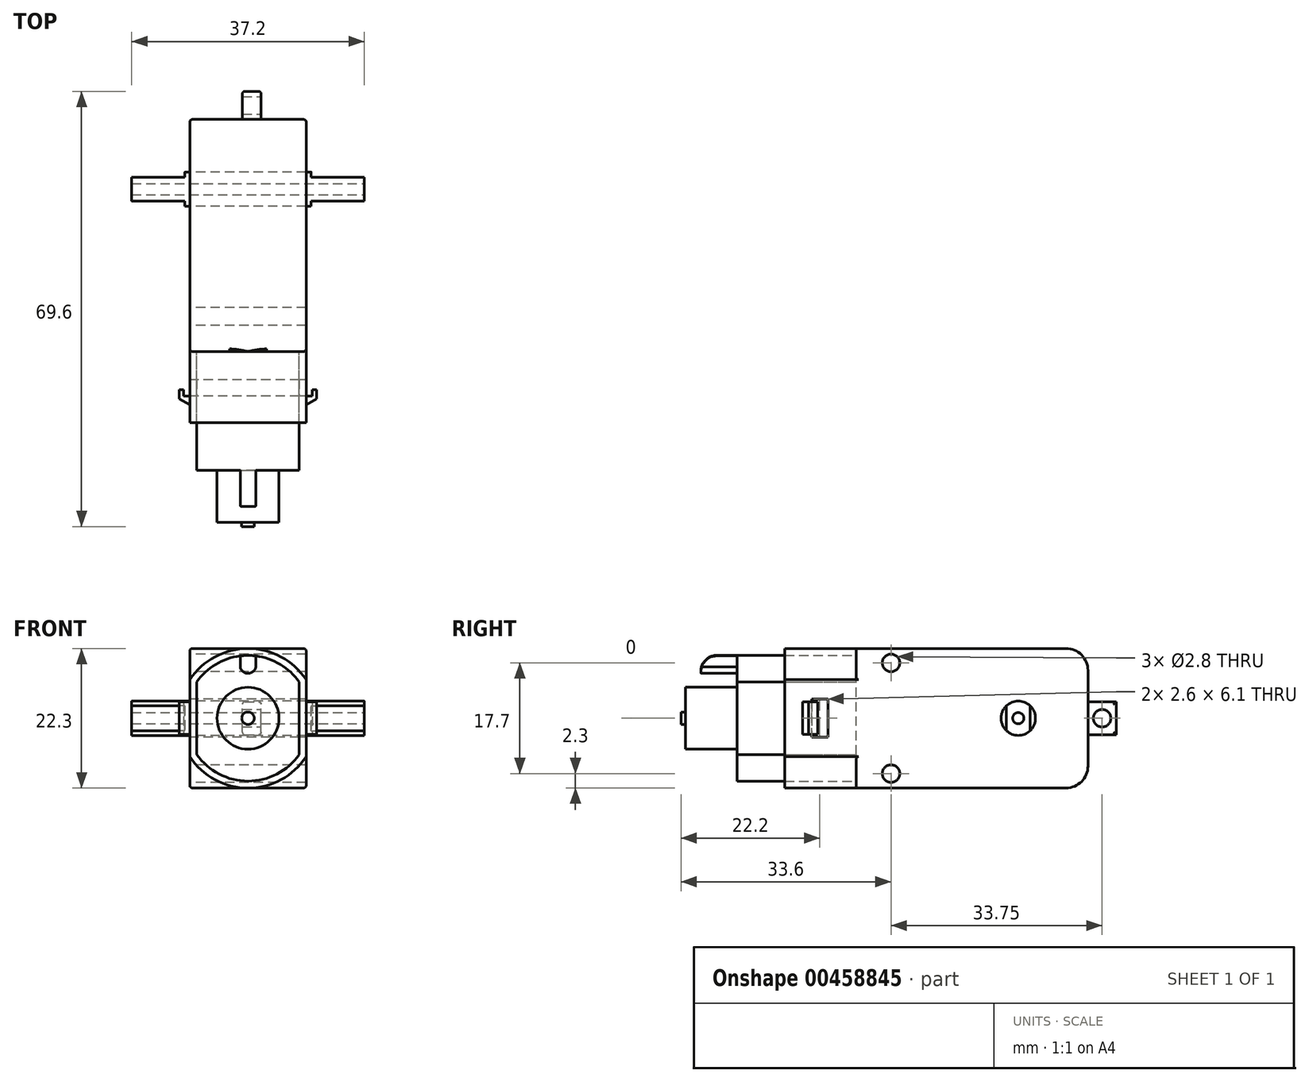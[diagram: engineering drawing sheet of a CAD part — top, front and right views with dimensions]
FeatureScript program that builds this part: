
annotation { "Feature Type Name" : "Feature", "Feature Type Description" : "" }
export const myFeature = defineFeature(function(context is Context, id is Id, definition is map)
    precondition{}
    {
        {
            var Q0;
            Q0=qCreatedBy(makeId("Front.planeOp"),FACE);
            var sketch = newSketch(context, id + "F0", { "sketchPlane" : qUnion([Q0])});
            skLineSegment(sketch, "E0.bottom", {"start": v(9.3, -11.15) * mm, "end": v(-9.3, -11.15) * mm});
            skLineSegment(sketch, "E0.top", {"start": v(9.3, 11.15) * mm, "end": v(-9.3, 11.15) * mm});
            skLineSegment(sketch, "E0.left", {"start": v(9.3, -11.15) * mm, "end": v(9.3, 11.15) * mm});
            skLineSegment(sketch, "E0.right", {"start": v(-9.3, -11.15) * mm, "end": v(-9.3, 11.15) * mm});
            skPoint(sketch, "E0.middle", {"position": v(0, 0) * mm});
            skSolve(sketch);
        }
        {
            var Q0;
            Q0 = qSketchRegion(id + "F0", true);
            extrude(context, id + "F1", {"entities" : qUnion([Q0]), "depth" : 37.1 * mm});
        }
        {
            var Q0;
            Q0=makeQuery(id+"F1.opExtrude","SWEPT_FACE",FACE,{"disambiguationData":[OSD([sQuery(id+"F0.wireOp",EDGE,"E0.right")])]});
            var sketch = newSketch(context, id + "F2", { "sketchPlane" : qUnion([Q0])});
            skCircle(sketch, "E1", {"center": v(31.5, -8.85) * mm, "radius": 1.4 * mm});
            skLineSegment(sketch, "E2", {"start": v(0, 0) * mm, "end": v(37.1, 0) * mm, "construction": true});
            skCircle(sketch, "E3.MirrorC", {"center": v(31.5, 8.85) * mm, "radius": 1.4 * mm});
            skCircle(sketch, "E4", {"center": v(11.15, 0) * mm, "radius": 2.75 * mm});
            skSolve(sketch);
        }
        {
            var Q0;
            Q0=makeQuery(id+"F1.opExtrude","CAP_FACE",FACE,{"disambiguationData":[OSD([sQuery(id+"F0.wireOp",EDGE,"E0.bottom"),sQuery(id+"F0.wireOp",EDGE,"E0.top"),sQuery(id+"F0.wireOp",EDGE,"E0.left"),sQuery(id+"F0.wireOp",EDGE,"E0.right")])],"isStart":false});
            var sketch = newSketch(context, id + "F3", { "sketchPlane" : qUnion([Q0])});
            skArc(sketch, "E5", {"start": v(-9.3, -6.15) * mm, "mid": v(0, -11.15) * mm, "end": v(9.3, -6.15) * mm});
            skLineSegment(sketch, "E6.0", {"start": v(9.3, -6.15) * mm, "end": v(9.3, 6.15) * mm});
            skLineSegment(sketch, "E6.1", {"start": v(-9.3, -6.15) * mm, "end": v(-9.3, 6.15) * mm});
            skArc(sketch, "E7.trimOffspring", {"start": v(9.3, 6.15) * mm, "mid": v(0, 11.15) * mm, "end": v(-9.3, 6.15) * mm});
            skPoint(sketch, "E8.orphan", {"position": v(-9.3, 11.15) * mm});
            skPoint(sketch, "E9.orphan", {"position": v(9.3, 11.15) * mm});
            skPoint(sketch, "E10.orphan", {"position": v(9.3, -11.15) * mm});
            skPoint(sketch, "E11.orphan", {"position": v(-9.3, -11.15) * mm});
            skArc(sketch, "E12.0", {"start": v(8.2, 5.81) * mm, "mid": v(0, 10.05) * mm, "end": v(-8.2, 5.81) * mm});
            skLineSegment(sketch, "E12.1", {"start": v(8.2, -5.81) * mm, "end": v(8.2, 5.81) * mm});
            skArc(sketch, "E12.2", {"start": v(-8.2, -5.81) * mm, "mid": v(0, -10.05) * mm, "end": v(8.2, -5.81) * mm});
            skLineSegment(sketch, "E12.3", {"start": v(-8.2, -5.81) * mm, "end": v(-8.2, 5.81) * mm});
            skSolve(sketch);
        }
        {
            var Q0;
            Q0 = qSketchRegion(id + "F3", true);
            extrude(context, id + "F4", {"entities" : qUnion([Q0]), "operationType" : NewBodyOperationType.ADD, "depth" : 11.4 * mm});
        }
        {
            var Q0;
            {var subQ0=sQuery(id+"F0.wireOp",EDGE,"F8vdl7xD-wS4J-gisc-z2d9-TpghqO1zXRkm");Q0=makeQuery(id+"F4.boolean.opBoolean","SPLIT",FACE,{"disambiguationData":[TD([makeQuery(id+"F1.opExtrude","SWEPT_FACE",FACE,{"disambiguationData":[OSD([subQ0])]}),makeQuery(id+"F4.opExtrude","SWEPT_FACE",FACE,{"disambiguationData":[OSD([sQuery(id+"F3.wireOp",EDGE,"E12.0")])]}),makeQuery(id+"F4.opExtrude","SWEPT_FACE",FACE,{"disambiguationData":[OSD([sQuery(id+"F3.wireOp",EDGE,"E12.1")])]}),makeQuery(id+"F4.opExtrude","SWEPT_FACE",FACE,{"disambiguationData":[OSD([sQuery(id+"F3.wireOp",EDGE,"E12.2")])]}),makeQuery(id+"F4.opExtrude","SWEPT_FACE",FACE,{"disambiguationData":[OSD([sQuery(id+"F3.wireOp",EDGE,"E12.3")])]})])],"derivedFrom":makeQuery(id+"F1.opExtrude","CAP_FACE",FACE,{"disambiguationData":[OSD([sQuery(id+"F0.wireOp",EDGE,"E0.bottom"),sQuery(id+"F0.wireOp",EDGE,"E0.top"),sQuery(id+"F0.wireOp",EDGE,"E0.left"),sQuery(id+"F0.wireOp",EDGE,"E0.right"),subQ0])],"isStart":false})});}
            var sketch = newSketch(context, id + "F5", { "sketchPlane" : qUnion([Q0])});
            skLineSegment(sketch, "E13.0", {"start": v(-8.2, -5.81) * mm, "end": v(-8.2, 5.81) * mm});
            skArc(sketch, "E13.1", {"start": v(8.2, 5.81) * mm, "mid": v(0, 10.05) * mm, "end": v(-8.2, 5.81) * mm});
            skLineSegment(sketch, "E13.2", {"start": v(8.2, -5.81) * mm, "end": v(8.2, 5.81) * mm});
            skArc(sketch, "E13.3", {"start": v(-8.2, -5.81) * mm, "mid": v(0, -10.05) * mm, "end": v(8.2, -5.81) * mm});
            skSolve(sketch);
        }
        {
            var Q0;
            Q0 = qSketchRegion(id + "F5", true);
            extrude(context, id + "F6", {"entities" : qUnion([Q0]), "depth" : 24.8 * mm});
        }
        {
            var Q0;
            Q0 = qSketchRegion(id + "F2", true);
            extrude(context, id + "F7", {"entities" : qUnion([Q0]), "operationType" : NewBodyOperationType.REMOVE, "oppositeDirection" : true, "depth" : 25 * mm});
        }
        {
            var Q0;
            Q0=qCreatedBy(makeId("Right.planeOp"),FACE);
            var sketch = newSketch(context, id + "F8", { "sketchPlane" : qUnion([Q0])});
            skCircle(sketch, "E14", {"center": v(-11.15, 0) * mm, "radius": 2.75 * mm});
            skSolve(sketch);
        }
        {
            var Q0;
            Q0 = qSketchRegion(id + "F8", true);
            extrude(context, id + "F9", {"entities" : qUnion([Q0]), "depth" : 37.2 * mm, "symmetric" : true});
        }
        {
            var Q0;
            Q0=makeQuery(id+"F9.opExtrude","CAP_FACE",FACE,{"disambiguationData":[OSD([sQuery(id+"F8.wireOp",EDGE,"E14")])],"isStart":false});
            var sketch = newSketch(context, id + "F10", { "sketchPlane" : qUnion([Q0])});
            skLineSegment(sketch, "E15", {"start": v(-9.25, -1.99) * mm, "end": v(-9.25, 1.99) * mm});
            skLineSegment(sketch, "E16", {"start": v(-13.05, -1.99) * mm, "end": v(-13.05, 1.99) * mm});
            skPoint(sketch, "E17.start.orphan", {"position": v(-8.4, 0) * mm});
            skArc(sketch, "E18.0", {"start": v(-9.25, -1.99) * mm, "mid": v(-8.4, 0) * mm, "end": v(-9.25, 1.99) * mm});
            skArc(sketch, "E19.trimOffspring", {"start": v(-13.05, 1.99) * mm, "mid": v(-13.9, 0) * mm, "end": v(-13.05, -1.99) * mm});
            skSolve(sketch);
        }
        {
            var Q0;
            Q0 = qSketchRegion(id + "F10", true);
            extrude(context, id + "F11", {"entities" : qUnion([Q0]), "operationType" : NewBodyOperationType.REMOVE, "oppositeDirection" : true, "depth" : 8.5 * mm});
        }
        {
            var Q0;
            Q0=makeQuery(id+"F9.opExtrude","CAP_FACE",FACE,{"disambiguationData":[OSD([sQuery(id+"F8.wireOp",EDGE,"E14")])],"isStart":true});
            var sketch = newSketch(context, id + "F12", { "sketchPlane" : qUnion([Q0])});
            skLineSegment(sketch, "E20", {"start": v(9.25, 1.99) * mm, "end": v(9.25, -1.99) * mm});
            skLineSegment(sketch, "E21", {"start": v(13.05, 1.99) * mm, "end": v(13.05, -1.99) * mm});
            skPoint(sketch, "E22.start.orphan", {"position": v(9.25, 0) * mm});
            skPoint(sketch, "E23.start.orphan", {"position": v(13.05, 0) * mm});
            skArc(sketch, "E24.0", {"start": v(9.25, 1.99) * mm, "mid": v(11.15, -2.75) * mm, "end": v(13.05, 1.99) * mm});
            skSolve(sketch);
        }
        {
            var Q0;
            Q0 = qSketchRegion(id + "F12", true);
            extrude(context, id + "F13", {"entities" : qUnion([Q0]), "operationType" : NewBodyOperationType.REMOVE, "oppositeDirection" : true, "depth" : 8.5 * mm});
        }
        {
            var Q0;
            Q0=makeQuery(id+"F1.opExtrude","CAP_FACE",FACE,{"disambiguationData":[OSD([sQuery(id+"F0.wireOp",EDGE,"E0.bottom"),sQuery(id+"F0.wireOp",EDGE,"E0.top"),sQuery(id+"F0.wireOp",EDGE,"E0.left"),sQuery(id+"F0.wireOp",EDGE,"E0.right")])],"isStart":true});
            var sketch = newSketch(context, id + "F14", { "sketchPlane" : qUnion([Q0])});
            skPoint(sketch, "E25.middle", {"position": v(-0.6, 0) * mm});
            skLineSegment(sketch, "E26.bottom", {"start": v(0.9, -2.63) * mm, "end": v(-2.1, -2.63) * mm});
            skLineSegment(sketch, "E26.top", {"start": v(0.9, 2.63) * mm, "end": v(-2.1, 2.63) * mm});
            skLineSegment(sketch, "E26.left", {"start": v(0.9, -2.63) * mm, "end": v(0.9, 2.63) * mm});
            skLineSegment(sketch, "E26.right", {"start": v(-2.1, -2.63) * mm, "end": v(-2.1, 2.63) * mm});
            skSolve(sketch);
        }
        {
            var Q0;
            Q0 = qSketchRegion(id + "F14", true);
            extrude(context, id + "F15", {"entities" : qUnion([Q0]), "operationType" : NewBodyOperationType.ADD, "depth" : 4.5 * mm});
        }
        {
            var Q0;
            Q0=makeQuery(id+"F4.boolean.opBoolean","MERGE",FACE,{"derivedFrom":[makeQuery(id+"F1.opExtrude","SWEPT_FACE",FACE,{"disambiguationData":[OSD([sQuery(id+"F0.wireOp",EDGE,"E0.right")])]}),makeQuery(id+"F4.opExtrude","SWEPT_FACE",FACE,{"disambiguationData":[OSD([sQuery(id+"F3.wireOp",EDGE,"E6.1")])]})]});
            var sketch = newSketch(context, id + "F16", { "sketchPlane" : qUnion([Q0])});
            skLineSegment(sketch, "E27.bottom", {"start": v(41.6, -3.05) * mm, "end": v(44.2, -3.05) * mm});
            skLineSegment(sketch, "E27.top", {"start": v(41.6, 3.05) * mm, "end": v(44.2, 3.05) * mm});
            skLineSegment(sketch, "E27.left", {"start": v(41.6, -3.05) * mm, "end": v(41.6, 3.05) * mm});
            skLineSegment(sketch, "E27.right", {"start": v(44.2, -3.05) * mm, "end": v(44.2, 3.05) * mm});
            skPoint(sketch, "E27.middle", {"position": v(42.9, 0) * mm});
            skSolve(sketch);
        }
        {
            var Q0;
            Q0=makeQuery(id+"F6.opExtrude","CAP_FACE",FACE,{"disambiguationData":[OSD([sQuery(id+"F5.wireOp",EDGE,"E13.0"),sQuery(id+"F5.wireOp",EDGE,"E13.1"),sQuery(id+"F5.wireOp",EDGE,"E13.2"),sQuery(id+"F5.wireOp",EDGE,"E13.3")])],"isStart":false});
            var sketch = newSketch(context, id + "F17", { "sketchPlane" : qUnion([Q0])});
            skCircle(sketch, "E28", {"center": v(0, 0) * mm, "radius": 4.95 * mm});
            skCircle(sketch, "E29", {"center": v(0, 0) * mm, "radius": 1 * mm});
            skSolve(sketch);
        }
        {
            var Q0;
            Q0=makeQuery(id+"F17.imprint","IMPRINT",FACE,{"disambiguationData":[TD([[makeQuery(id+"F17.imprint","IMPRINT",EDGE,{"derivedFrom":sQuery(id+"F17.wireOp",EDGE,"E29")}),1.0]])]});
            extrude(context, id + "F18", {"entities" : qUnion([Q0]), "operationType" : NewBodyOperationType.ADD, "depth" : 3.2 * mm});
        }
        {
            var Q0;
            Q0=makeQuery(id+"F17.imprint","IMPRINT",FACE,{"disambiguationData":[TD([[makeQuery(id+"F17.imprint","IMPRINT",EDGE,{"derivedFrom":sQuery(id+"F17.wireOp",EDGE,"E28")}),1.0]])]});
            extrude(context, id + "F19", {"entities" : qUnion([Q0]), "operationType" : NewBodyOperationType.ADD, "depth" : 2.5 * mm});
        }
        {
            var Q0;
            Q0=makeQuery(id+"F17.imprint","IMPRINT",FACE,{"disambiguationData":[TD([[makeQuery(id+"F17.imprint","IMPRINT",EDGE,{"derivedFrom":sQuery(id+"F17.wireOp",EDGE,"E28")}),-1.0]])]});
            var sketch = newSketch(context, id + "F20", { "sketchPlane" : qUnion([Q0])});
            skArc(sketch, "E30.0", {"start": v(-1.25, -9.97) * mm, "mid": v(0, -10.05) * mm, "end": v(1.25, -9.97) * mm});
            skLineSegment(sketch, "E31", {"start": v(-1.25, -9.97) * mm, "end": v(-1.25, -8.18) * mm});
            skLineSegment(sketch, "E32", {"start": v(1.25, -9.97) * mm, "end": v(1.25, -8.18) * mm});
            skArc(sketch, "E33", {"start": v(1.25, -8.18) * mm, "mid": v(0, -7.18) * mm, "end": v(-1.25, -8.18) * mm});
            skArc(sketch, "E34.MirrorCS", {"start": v(1.25, 8.18) * mm, "mid": v(0, 7.18) * mm, "end": v(-1.25, 8.18) * mm});
            skLineSegment(sketch, "E35.MirrorCS", {"start": v(1.25, 9.97) * mm, "end": v(1.25, 8.18) * mm});
            skLineSegment(sketch, "E36.MirrorCS", {"start": v(-1.25, 9.97) * mm, "end": v(-1.25, 8.18) * mm});
            skArc(sketch, "E37.0", {"start": v(1.25, 9.97) * mm, "mid": v(0, 10.05) * mm, "end": v(-1.25, 9.97) * mm});
            skPoint(sketch, "E38.orphan", {"position": v(-8.2, 5.81) * mm});
            skPoint(sketch, "E39.orphan", {"position": v(8.2, 5.81) * mm});
            skPoint(sketch, "E40.orphan", {"position": v(8.2, -5.81) * mm});
            skPoint(sketch, "E41.orphan", {"position": v(-8.2, -5.81) * mm});
            skSolve(sketch);
        }
        {
            var Q0;
            Q0=makeQuery(id+"F16.imprint","IMPRINT",FACE,{"disambiguationData":[TD([[makeQuery(id+"F16.imprint","IMPRINT",EDGE,{"derivedFrom":sQuery(id+"F16.wireOp",EDGE,"E27.bottom")}),1.0]])]});
            extrude(context, id + "F21", {"entities" : qUnion([Q0]), "operationType" : NewBodyOperationType.REMOVE, "oppositeDirection" : true, "depth" : 25 * mm});
        }
        {
            var Q0;
            Q0=qCreatedBy(makeId("Top.planeOp"),FACE);
            var sketch = newSketch(context, id + "F22", { "sketchPlane" : qUnion([Q0])});
            skPoint(sketch, "E42.0", {"position": v(-9.3, -44.2) * mm});
            skLineSegment(sketch, "E43", {"start": v(-9.3, -44.2) * mm, "end": v(-9.3, -45.65) * mm});
            skLineSegment(sketch, "E44", {"start": v(-9.3, -45.65) * mm, "end": v(-11, -44.7) * mm});
            skLineSegment(sketch, "E45", {"start": v(-11, -44.7) * mm, "end": v(-11, -43.2) * mm});
            skLineSegment(sketch, "E46", {"start": v(-11, -43.2) * mm, "end": v(-10.3, -43.2) * mm});
            skLineSegment(sketch, "E47", {"start": v(-10.3, -43.2) * mm, "end": v(-10.3, -44.2) * mm});
            skLineSegment(sketch, "E48", {"start": v(-10.3, -44.2) * mm, "end": v(-9.3, -44.2) * mm});
            skSolve(sketch);
        }
        {
            var Q0;
            Q0=makeQuery(id+"F22.imprint","IMPRINT",FACE,{"disambiguationData":[TD([[makeQuery(id+"F22.imprint","IMPRINT",EDGE,{"derivedFrom":sQuery(id+"F22.wireOp",EDGE,"E43")}),-1.0]])]});
            extrude(context, id + "F23", {"entities" : qUnion([Q0]), "operationType" : NewBodyOperationType.ADD, "depth" : 5.2 * mm, "symmetric" : true});
        }
        {
            var Q0;
            Q0=makeQuery(id+"F9.opExtrude","CAP_FACE",FACE,{"disambiguationData":[OSD([sQuery(id+"F8.wireOp",EDGE,"E14")])],"isStart":false});
            var sketch = newSketch(context, id + "F24", { "sketchPlane" : qUnion([Q0])});
            skCircle(sketch, "E49", {"center": v(-11.15, 0) * mm, "radius": 0.9 * mm});
            skSolve(sketch);
        }
        {
            var Q0;
            Q0 = qSketchRegion(id + "F24", true);
            extrude(context, id + "F25", {"entities" : qUnion([Q0]), "operationType" : NewBodyOperationType.REMOVE, "endBound" : BoundingType.THROUGH_ALL, "oppositeDirection" : true, "depth" : 25 * mm});
        }
        {
            var Q0;
            Q0=qCreatedBy(makeId("Top.planeOp"),FACE);
            var sketch = newSketch(context, id + "F26", { "sketchPlane" : qUnion([Q0])});
            skPoint(sketch, "E50.0", {"position": v(9.3, -44.2) * mm});
            skLineSegment(sketch, "E51", {"start": v(9.3, -44.2) * mm, "end": v(9.3, -45.65) * mm});
            skLineSegment(sketch, "E52", {"start": v(9.3, -45.65) * mm, "end": v(11, -44.7) * mm});
            skLineSegment(sketch, "E53", {"start": v(11, -44.7) * mm, "end": v(11, -43.2) * mm});
            skLineSegment(sketch, "E54", {"start": v(11, -43.2) * mm, "end": v(10.3, -43.2) * mm});
            skLineSegment(sketch, "E55", {"start": v(10.3, -43.2) * mm, "end": v(10.3, -44.2) * mm});
            skLineSegment(sketch, "E56", {"start": v(10.3, -44.2) * mm, "end": v(9.3, -44.2) * mm});
            skSolve(sketch);
        }
        {
            var Q0;
            Q0=makeQuery(id+"F26.imprint","IMPRINT",FACE,{"disambiguationData":[TD([[makeQuery(id+"F26.imprint","IMPRINT",EDGE,{"derivedFrom":sQuery(id+"F26.wireOp",EDGE,"E51")}),1.0]])]});
            extrude(context, id + "F27", {"entities" : qUnion([Q0]), "operationType" : NewBodyOperationType.ADD, "depth" : 5.2 * mm, "symmetric" : true});
        }
        {
            var Q0;
            Q0=makeQuery(id+"F20.imprint","IMPRINT",FACE,{"disambiguationData":[TD([[makeQuery(id+"F20.imprint","IMPRINT",EDGE,{"derivedFrom":sQuery(id+"F20.wireOp",EDGE,"E34.MirrorCS")}),-1.0]])]});
            var Q1;
            Q1=makeQuery(id+"F20.imprint","IMPRINT",FACE,{"disambiguationData":[TD([[makeQuery(id+"F20.imprint","IMPRINT",EDGE,{"derivedFrom":sQuery(id+"F20.wireOp",EDGE,"E30.0")}),1.0]])]});
            extrude(context, id + "F28", {"entities" : qUnion([Q0, Q1]), "operationType" : NewBodyOperationType.REMOVE, "oppositeDirection" : true, "depth" : 5.8 * mm});
        }
        {
            var Q0;
            Q0=makeQuery(id+"F15.opExtrude","SWEPT_FACE",FACE,{"disambiguationData":[OSD([sQuery(id+"F14.wireOp",EDGE,"E26.right")])]});
            var sketch = newSketch(context, id + "F29", { "sketchPlane" : qUnion([Q0])});
            skPoint(sketch, "E57.end.orphan", {"position": v(-4.5, 0) * mm});
            skPoint(sketch, "E57.start.orphan", {"position": v(-3.65, 0) * mm});
            skPoint(sketch, "E58.start.orphan", {"position": v(-0.85, 0) * mm});
            skCircle(sketch, "E59", {"center": v(2.25, 0) * mm, "radius": 1.4 * mm});
            skLineSegment(sketch, "E60", {"start": v(2.25, 2.63) * mm, "end": v(2.25, 0) * mm, "construction": true});
            skLineSegment(sketch, "E61", {"start": v(4.5, 0) * mm, "end": v(2.25, 0) * mm, "construction": true});
            skSolve(sketch);
        }
        {
            var Q0;
            Q0=makeQuery(id+"F29.imprint","IMPRINT",FACE,{"disambiguationData":[TD([[makeQuery(id+"F29.imprint","IMPRINT",EDGE,{"derivedFrom":sQuery(id+"F29.wireOp",EDGE,"E59")}),1.0]])]});
            extrude(context, id + "F30", {"entities" : qUnion([Q0]), "operationType" : NewBodyOperationType.REMOVE, "endBound" : BoundingType.THROUGH_ALL, "oppositeDirection" : true, "depth" : 25 * mm, "offsetDistance" : 25 * mm});
        }
        {
            var Q0;
            Q0=makeQuery(id+"F1.opExtrude","CAP_EDGE",EDGE,{"disambiguationData":[OSD([sQuery(id+"F0.wireOp",EDGE,"E0.top")])],"isStart":true});
            var Q1;
            Q1=makeQuery(id+"F1.opExtrude","CAP_EDGE",EDGE,{"disambiguationData":[OSD([sQuery(id+"F0.wireOp",EDGE,"E0.bottom")])],"isStart":true});
            fillet(context, id + "F31", {"entities" : qUnion([Q0, Q1]), "radius" : 3.5 * mm, "tangentPropagation" : true, "allowEdgeOverflow" : false});
        }
        {
            var Q0;
            {var subQ0=sQuery(id+"F0.wireOp",EDGE,"E0.right");var subQ1=sQuery(id+"F0.wireOp",EDGE,"E0.top");Q0=makeQuery(id+"F4.boolean.opBoolean","SPLIT",EDGE,{"disambiguationData":[TD([makeQuery(id+"F1.opExtrude","SWEPT_FACE",FACE,{"disambiguationData":[OSD([subQ0])]})])],"derivedFrom":makeQuery(id+"F1.opExtrude","CAP_EDGE",EDGE,{"disambiguationData":[OSD([subQ1])],"isStart":false})});}
            var Q1;
            {var subQ0=sQuery(id+"F0.wireOp",EDGE,"E0.left");var subQ1=sQuery(id+"F0.wireOp",EDGE,"E0.top");Q1=makeQuery(id+"F4.boolean.opBoolean","SPLIT",EDGE,{"disambiguationData":[TD([makeQuery(id+"F1.opExtrude","SWEPT_FACE",FACE,{"disambiguationData":[OSD([subQ0])]})])],"derivedFrom":makeQuery(id+"F1.opExtrude","CAP_EDGE",EDGE,{"disambiguationData":[OSD([subQ1])],"isStart":false})});}
            var Q2;
            {var subQ0=sQuery(id+"F0.wireOp",EDGE,"E0.left");var subQ1=sQuery(id+"F0.wireOp",EDGE,"E0.bottom");Q2=makeQuery(id+"F4.boolean.opBoolean","SPLIT",EDGE,{"disambiguationData":[TD([makeQuery(id+"F1.opExtrude","SWEPT_FACE",FACE,{"disambiguationData":[OSD([subQ0])]})])],"derivedFrom":makeQuery(id+"F1.opExtrude","CAP_EDGE",EDGE,{"disambiguationData":[OSD([subQ1])],"isStart":false})});}
            var Q3;
            {var subQ0=sQuery(id+"F0.wireOp",EDGE,"E0.right");var subQ1=sQuery(id+"F0.wireOp",EDGE,"E0.bottom");Q3=makeQuery(id+"F4.boolean.opBoolean","SPLIT",EDGE,{"disambiguationData":[TD([makeQuery(id+"F1.opExtrude","SWEPT_FACE",FACE,{"disambiguationData":[OSD([subQ0])]})])],"derivedFrom":makeQuery(id+"F1.opExtrude","CAP_EDGE",EDGE,{"disambiguationData":[OSD([subQ1])],"isStart":false})});}
            var Q4;
            {var subQ0=sQuery(id+"F0.wireOp",EDGE,"E0.right");var subQ1=sQuery(id+"F0.wireOp",EDGE,"E0.bottom");Q4=makeQuery(id+"F4.boolean.opBoolean","SPLIT",EDGE,{"disambiguationData":[TD([makeQuery(id+"F1.opExtrude","SWEPT_FACE",FACE,{"disambiguationData":[OSD([subQ1])]})])],"derivedFrom":makeQuery(id+"F1.opExtrude","CAP_EDGE",EDGE,{"disambiguationData":[OSD([subQ0])],"isStart":false})});}
            var Q5;
            {var subQ0=sQuery(id+"F0.wireOp",EDGE,"E0.left");var subQ1=sQuery(id+"F0.wireOp",EDGE,"E0.bottom");Q5=makeQuery(id+"F4.boolean.opBoolean","SPLIT",EDGE,{"disambiguationData":[TD([makeQuery(id+"F1.opExtrude","SWEPT_FACE",FACE,{"disambiguationData":[OSD([subQ1])]})])],"derivedFrom":makeQuery(id+"F1.opExtrude","CAP_EDGE",EDGE,{"disambiguationData":[OSD([subQ0])],"isStart":false})});}
            var Q6;
            {var subQ0=sQuery(id+"F0.wireOp",EDGE,"E0.left");var subQ1=sQuery(id+"F0.wireOp",EDGE,"E0.top");Q6=makeQuery(id+"F4.boolean.opBoolean","SPLIT",EDGE,{"disambiguationData":[TD([makeQuery(id+"F1.opExtrude","SWEPT_FACE",FACE,{"disambiguationData":[OSD([subQ1])]})])],"derivedFrom":makeQuery(id+"F1.opExtrude","CAP_EDGE",EDGE,{"disambiguationData":[OSD([subQ0])],"isStart":false})});}
            var Q7;
            {var subQ0=sQuery(id+"F0.wireOp",EDGE,"E0.right");var subQ1=sQuery(id+"F0.wireOp",EDGE,"E0.top");Q7=makeQuery(id+"F4.boolean.opBoolean","SPLIT",EDGE,{"disambiguationData":[TD([makeQuery(id+"F1.opExtrude","SWEPT_FACE",FACE,{"disambiguationData":[OSD([subQ1])]})])],"derivedFrom":makeQuery(id+"F1.opExtrude","CAP_EDGE",EDGE,{"disambiguationData":[OSD([subQ0])],"isStart":false})});}
            var Q8;
            Q8=makeQuery(id+"F1.opExtrude","SWEPT_EDGE",EDGE,{"disambiguationData":[OSD([sQuery(id+"F0.wireOp",EDGE,"E0.top"),sQuery(id+"F0.wireOp",EDGE,"E0.right")])]});
            var Q9;
            Q9=makeQuery(id+"F1.opExtrude","SWEPT_EDGE",EDGE,{"disambiguationData":[OSD([sQuery(id+"F0.wireOp",EDGE,"E0.bottom"),sQuery(id+"F0.wireOp",EDGE,"E0.left")])]});
            var Q10;
            Q10=makeQuery(id+"F15.opExtrude","SWEPT_EDGE",EDGE,{"disambiguationData":[OSD([sQuery(id+"F14.wireOp",EDGE,"E26.top"),sQuery(id+"F14.wireOp",EDGE,"E26.right")])]});
            var Q11;
            Q11=makeQuery(id+"F15.opExtrude","CAP_EDGE",EDGE,{"disambiguationData":[OSD([sQuery(id+"F14.wireOp",EDGE,"E26.right")])],"isStart":false});
            var Q12;
            Q12=makeQuery(id+"F15.opExtrude","SWEPT_EDGE",EDGE,{"disambiguationData":[OSD([sQuery(id+"F14.wireOp",EDGE,"E26.bottom"),sQuery(id+"F14.wireOp",EDGE,"E26.right")])]});
            var Q13;
            Q13=makeQuery(id+"F15.opExtrude","SWEPT_EDGE",EDGE,{"disambiguationData":[OSD([sQuery(id+"F14.wireOp",EDGE,"E26.top"),sQuery(id+"F14.wireOp",EDGE,"E26.left")])]});
            var Q14;
            Q14=makeQuery(id+"F15.opExtrude","CAP_EDGE",EDGE,{"disambiguationData":[OSD([sQuery(id+"F14.wireOp",EDGE,"E26.left")])],"isStart":false});
            var Q15;
            Q15=makeQuery(id+"F15.opExtrude","SWEPT_EDGE",EDGE,{"disambiguationData":[OSD([sQuery(id+"F14.wireOp",EDGE,"E26.bottom"),sQuery(id+"F14.wireOp",EDGE,"E26.left")])]});
            fillet(context, id + "F32", {"entities" : qUnion([Q0, Q1, Q2, Q3, Q4, Q5, Q6, Q7, Q8, Q9, Q10, Q11, Q12, Q13, Q14, Q15]), "radius" : .4 * mm, "tangentPropagation" : true, "allowEdgeOverflow" : false});
        }
        {
            var Q0;
            {var subQ0=sQuery(id+"F5.wireOp",EDGE,"E13.0");var subQ1=sQuery(id+"F5.wireOp",EDGE,"E13.1");Q0=makeQuery(id+"F28.boolean.opBoolean","SPLIT",EDGE,{"disambiguationData":[TD([makeQuery(id+"F6.opExtrude","SWEPT_FACE",FACE,{"disambiguationData":[OSD([subQ0])]})])],"derivedFrom":makeQuery(id+"F6.opExtrude","CAP_EDGE",EDGE,{"disambiguationData":[OSD([subQ1])],"isStart":false})});}
            var Q1;
            {var subQ0=sQuery(id+"F5.wireOp",EDGE,"E13.0");var subQ1=sQuery(id+"F5.wireOp",EDGE,"E13.3");Q1=makeQuery(id+"F28.boolean.opBoolean","SPLIT",EDGE,{"disambiguationData":[TD([makeQuery(id+"F6.opExtrude","SWEPT_FACE",FACE,{"disambiguationData":[OSD([subQ0])]})])],"derivedFrom":makeQuery(id+"F6.opExtrude","CAP_EDGE",EDGE,{"disambiguationData":[OSD([subQ1])],"isStart":false})});}
            var Q2;
            {var subQ0=sQuery(id+"F5.wireOp",EDGE,"E13.3");var subQ1=sQuery(id+"F5.wireOp",EDGE,"E13.2");Q2=makeQuery(id+"F28.boolean.opBoolean","SPLIT",EDGE,{"disambiguationData":[TD([makeQuery(id+"F6.opExtrude","SWEPT_FACE",FACE,{"disambiguationData":[OSD([subQ1])]})])],"derivedFrom":makeQuery(id+"F6.opExtrude","CAP_EDGE",EDGE,{"disambiguationData":[OSD([subQ0])],"isStart":false})});}
            var Q3;
            {var subQ0=sQuery(id+"F5.wireOp",EDGE,"E13.2");var subQ1=sQuery(id+"F5.wireOp",EDGE,"E13.1");Q3=makeQuery(id+"F28.boolean.opBoolean","SPLIT",EDGE,{"disambiguationData":[TD([makeQuery(id+"F6.opExtrude","SWEPT_FACE",FACE,{"disambiguationData":[OSD([subQ0])]})])],"derivedFrom":makeQuery(id+"F6.opExtrude","CAP_EDGE",EDGE,{"disambiguationData":[OSD([subQ1])],"isStart":false})});}
            fillet(context, id + "F33", {"entities" : qUnion([Q0, Q1, Q2, Q3]), "radius" : 2.5 * mm, "tangentPropagation" : true, "allowEdgeOverflow" : false});
        }
    });
